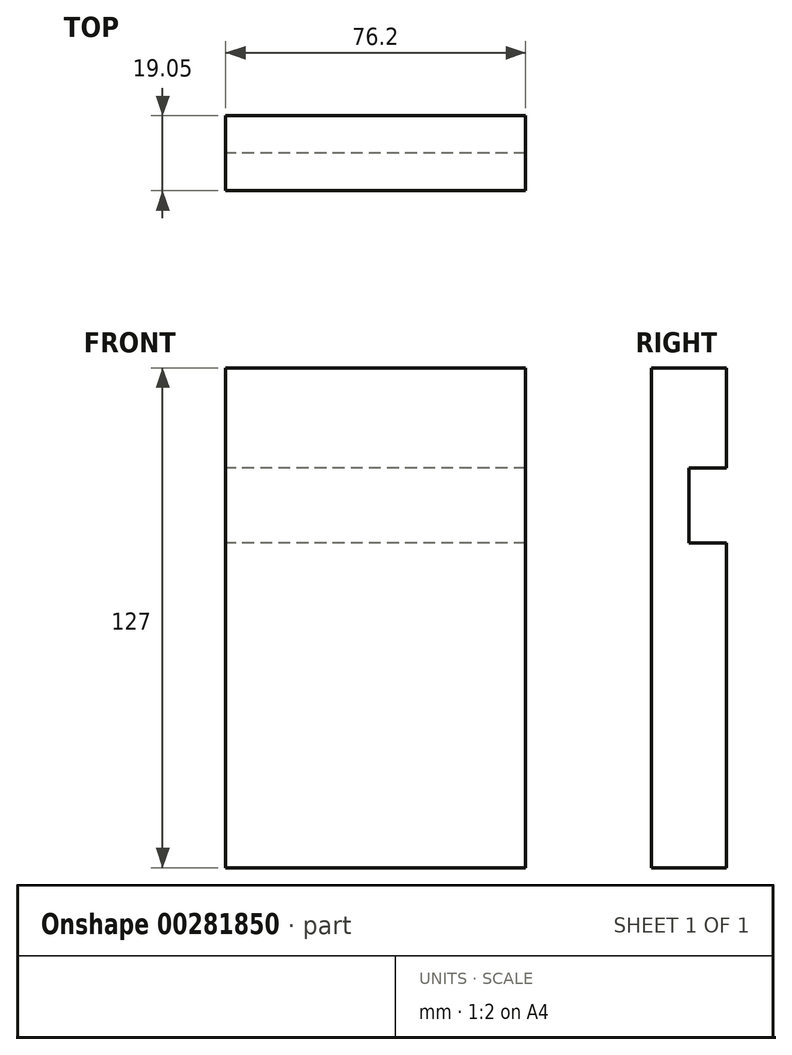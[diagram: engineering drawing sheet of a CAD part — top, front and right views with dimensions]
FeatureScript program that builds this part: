
annotation { "Feature Type Name" : "Feature", "Feature Type Description" : "" }
export const myFeature = defineFeature(function(context is Context, id is Id, definition is map)
    precondition{}
    {
        {
            var Q0;
            Q0=qCreatedBy(makeId("Right.planeOp"),FACE);
            var sketch = newSketch(context, id + "F0", { "sketchPlane" : qUnion([Q0])});
            skLineSegment(sketch, "E0", {"start": v(0, 0) * mm, "end": v(0, 127) * mm});
            skLineSegment(sketch, "E1", {"start": v(0, 127) * mm, "end": v(19.05, 127) * mm});
            skLineSegment(sketch, "E2", {"start": v(19.05, 127) * mm, "end": v(19.05, 101.6) * mm});
            skLineSegment(sketch, "E3", {"start": v(19.05, 101.6) * mm, "end": v(19.05, 105.87) * mm});
            skLineSegment(sketch, "E4", {"start": v(19.05, 101.6) * mm, "end": v(9.53, 101.6) * mm});
            skLineSegment(sketch, "E5", {"start": v(9.53, 101.6) * mm, "end": v(9.53, 82.55) * mm});
            skLineSegment(sketch, "E6", {"start": v(9.53, 82.55) * mm, "end": v(19.05, 82.55) * mm});
            skLineSegment(sketch, "E7", {"start": v(19.05, 82.55) * mm, "end": v(19.05, 0) * mm});
            skLineSegment(sketch, "E8", {"start": v(19.05, 0) * mm, "end": v(0, 0) * mm});
            skSolve(sketch);
        }
        {
            var Q0;
            Q0 = qSketchRegion(id + "F0", true);
            extrude(context, id + "F1", {"entities" : qUnion([Q0]), "depth" : 76.2 * mm});
        }
    });
